# Revit family: Domotics-SerieCivili-GEWISS-27COMBI_SYSTEM-IP40_PRESA_GER
name_source: partatom
category: Apparecchi elettrici
revit_build: Autodesk Revit 2016 (Build: 20161004_0715(x64)
units: mm (PartAtom-declared; Revit-internal decimal feet)

## family parameters
Condiviso = No
Host = Superficie
Mantenere orientamento annotazione = Sì
Punto di calcolo locali = Sì
Quota connettore circolare = Usa diametro
Taglio con vuoti quando caricato = No
Tipo di parte = Normale

## types (1)
- Domotics-SerieCivili-GEWISS-27COMBI_SYSTEM-IP40_PRESA_GER
    Caratteristiche = Standard Tedesco
    Carico apparente = 0 VA
    Catalogo = DOMOTICS
    Catalogo Serie = 27COMBI
    Classe isolamento = II
    Codice EAN = 8011564095427
    Codice Electrocod = 0131
    Colore = Grigio RAL 7035
    Coppia serraggio viti = 0,8NM
    Descrizione = PRESA STD TED.2P+T 16A PROTETTA
    Descrizione: = Presa 2P+T - 16 A
    Dim. esterne BxHxP (mm) = 66x82x55
    Glow Wire Test = 650°C
    Grado di protezione = IP40
    IDF = 62b6f017-263e-4f17-99d7-c0e391134cba
    IDT = d2cc88c2-2bd0-4b6a-a7a0-6ff77e855ea8
    Immagine tipo = GW27814.jpg
    Modello = GW27814
    N. fori Ã˜ 23 con passacavo = 1
    N. fori Ã˜ 23 sfondabili: = Laterali 3 / Sul fondo 1
    N. poli = 1
    Norma di riferimento = IEC 60884-1
    Norma di riferimento: = IEC 60884-1
    Produttore = GEWISS S.p.A.
    Prospetto di default = 1219 mm
    SEO = Contenitore
    Scheda Tecnica = https://www.gewiss.com
    TXT ELETTRICO = 16
    Temperatura di installazione = -25 +60 °C
    Tensione = 250 V ac
    Tensione: = 250 V ac
    Termopressione con biglia = 70 °C
    Tipo sfondabili = Asportabili con utensile
    URL = https://www.gewiss.com
    Versione file RFA = 19.4
    Viti coperchio = Acciaio resistente alla corrosione
    Volt = 230 V

## geometry (parser evidence)
native form markers: Sweep x1
no freeform markers — native parametric forms only
